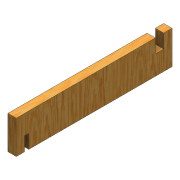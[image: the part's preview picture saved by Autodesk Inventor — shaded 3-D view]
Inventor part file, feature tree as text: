
AUTODESK INVENTOR PART (.ipt)
format: ipt  version: 2016 (Build 200138000, 138)  size: 118,272 bytes
history: native  units: mm
features: extrude x1, sketch x1
ambient origin geometry x8: Origin, YZ Plane, XZ Plane, XY Plane, X Axis, Y Axis, Z Axis, Center Point
bodies: Solid1 (feature_tree)
feature tree (2):
  extrude  "Extrusion1"  Depth=3.0mm TaperAngle=0.0deg
  sketch  "Sketch1"  dims[d0=56.0mm d2=3.0mm d3=0.0mm d4=3.0mm d5=5.0mm d6=3.0mm d8=5.0mm d9=3.0mm d11=12.0mm d12=0.0mm d13=0.0mm]
